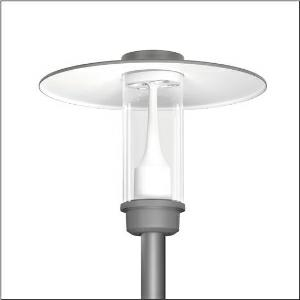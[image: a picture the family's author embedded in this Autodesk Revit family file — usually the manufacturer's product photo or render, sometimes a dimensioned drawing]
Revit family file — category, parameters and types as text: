
# Revit family: litepole_2_iq___pl1_2s_5xa5425of14h_0dca
name_source: partatom
category: Lighting Fixtures
units: mm (PartAtom-declared; Revit-internal decimal feet)

## family parameters
Cut with Voids When Loaded = No
Host = Face
Light Source = No
Part Type = Normal
Room Calculation Point = No
Round Connector Dimension = Use Diameter
Shared = No

## types (1)
- --- (1 x LED, 3000 lm, 21.8 W, 2700K)
    Apparent Load = 22 VA
    CIE Flux Codes = 22 60 92 98 100
    Color Rendering = 70
    Color Temperature = 2700K
    Default Elevation = 1800 mm
    Description = Litepole 2 iQ, mast luminaire, Module 540 iQ-SR, primary light control with 3 zone facetted reflector, of plastic, silver coated, highly specular, structured, primary optical cover: cover, of PMMA, transparent, light distribution: PL1.2s, light emission: direct distribution, primary light characteristic: symmetric, installation type: post-top, LED, High Power LED, rated luminous flux: 2.990lm, luminous efficacy: 137lm/W, light colour: 727, colour temperature: 2700K, control gear: iQ Street-Remote, control: pre-setting: logarithmic dimming characteristic, Street-Remote, Auto-Match, Temp-Guard, Lumen-Switch, Night-Set, Smart-Wire, Light-Fading, Desk-Remote (wireless, voltage-free reading and setting of iQ features in the workshop via application-optimized NFC function/RFID function), optimised constant luminous flux control (CLO 2.0), with terminal, 6-pole, max. 2.5mm², mains connection: 230..240V, AC, 50/60Hz, start of lifetime: 22W, end of service life: 23W, reduction: 11W, luminaire housing, upper part, of aluminium, coated, Siteco® metallic grey (DB 702S), diameter: 750mm, height: 590mm, spigot size: d x l = 76 x 70mm (post-top) | with reducer (optional accessory) 60 x 70mm, mounting height: 3..5m, post-top mast mounting element, of diecast aluminium, coated, Siteco® metallic grey (DB 702S), Module 540 iQ-SR, traffic white (RAL 9016), equipment: standard, protection rating (complete): IP65, insulation class (complete): insulation class II (safety insulation), certification: CE, ENEC, VDE, packaging unit: 1 piece

Light Distribution: PL1.2s
    Height = 590 mm
    Lamp = 1 x LED
    Lamp Light Flux = 3000 lm
    Lamp Power = 21.8 W
    Lamp count = 1
    Length = 750 mm
    Luminous efficacy = 138 lm/W
    Manufacturer = Siteco
    ModVariant = No
    Model = 5XA5425OF14H
    Number of Poles = 1
    OnlyDefault = Yes
    Power Factor = 1
    Product Name = Litepole 2 iQ | PL1.2s
    Product group = mast luminaire | pylon top
    ProductGroupID = 6100
    Protection Class = Protection class II
    Protection Degree = IP 65
    RLX_Detail_Level = 1
    RLX_Emergency_Light_Flux = 0 lm
    RLX_Emergency_Type = 0
    RLX_Emergency_Type_DB = No
    RlxData = <blob elided: 29409 chars, md5=571aeac8>
    Socket = socket
    Standby Power = 0 W
    System Light Flux = 3000 lm
    System Power = 22 W
    Type Comments = factory setting: luminous flux: 100 % | dim-lin: 254 | 456 mA
    Type Image = l_1006518.jpg
    URL = http://relux.com
    VarID = @adj_166017
    Voltage = 0 V
    Weight = 0.00 kg
    Width = 0 mm  [stored 0 ft]

note: [stored X ft] marks values corroborated as IEEE doubles in the binary element streams (Revit-internal decimal feet)

## geometry (parser evidence)
native form markers: Blend x4, Sweep x10
no freeform markers — native parametric forms only
